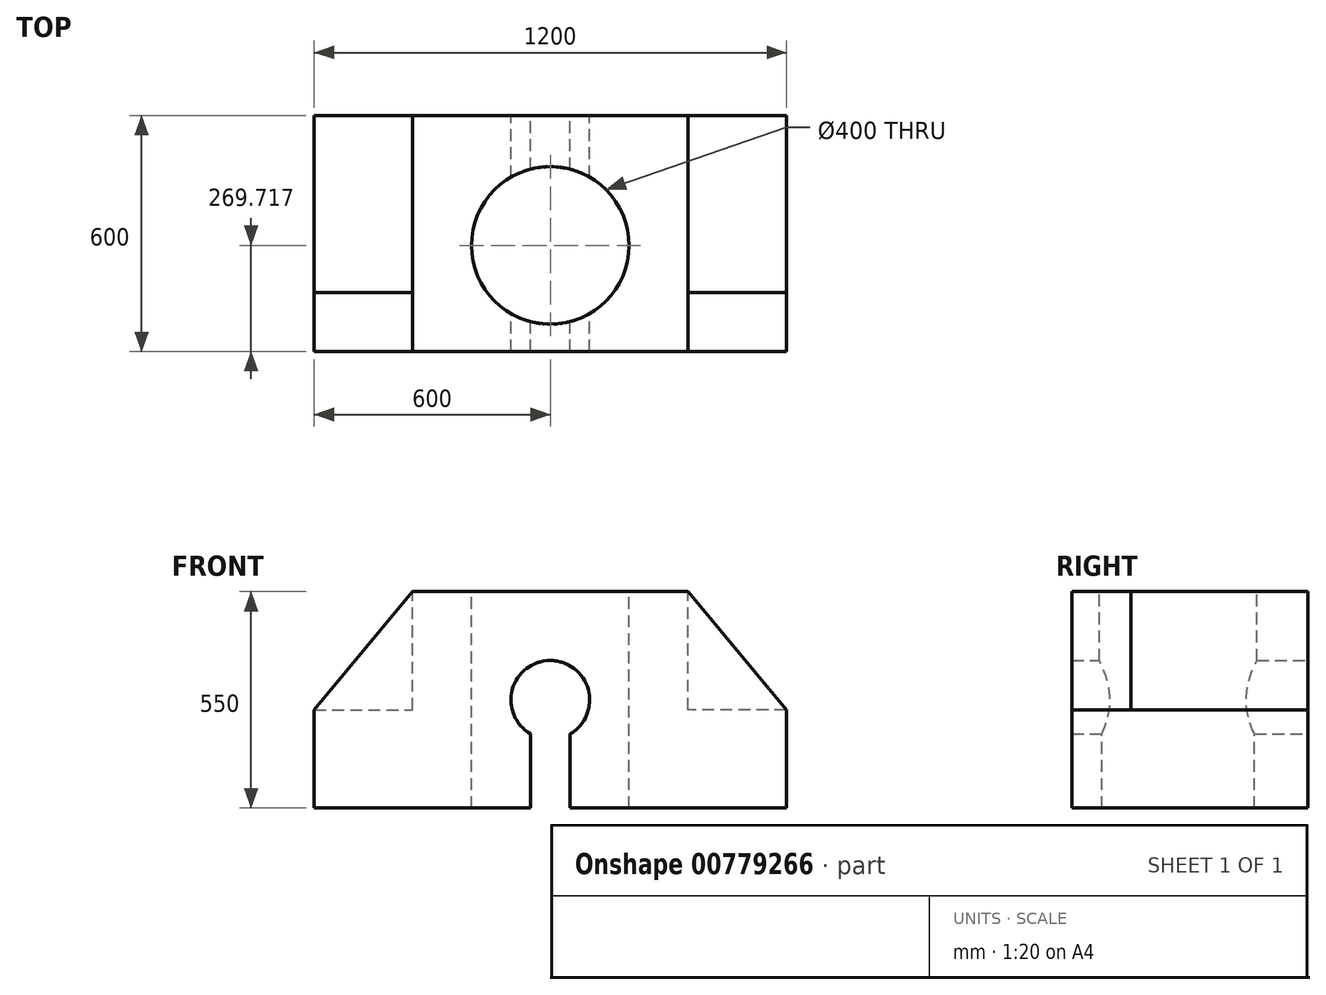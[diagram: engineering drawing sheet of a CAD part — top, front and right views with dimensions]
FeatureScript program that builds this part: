
annotation { "Feature Type Name" : "Feature", "Feature Type Description" : "" }
export const myFeature = defineFeature(function(context is Context, id is Id, definition is map)
    precondition{}
    {
        {
            var Q0;
            Q0=qCreatedBy(makeId("Front.planeOp"),FACE);
            var sketch = newSketch(context, id + "F0", { "sketchPlane" : qUnion([Q0])});
            skLineSegment(sketch, "E0.bottom", {"start": v(-68.7, 40.93) * mm, "end": v(68.7, 40.93) * mm});
            skLineSegment(sketch, "E0.top", {"start": v(-68.7, -40.93) * mm, "end": v(68.7, -40.93) * mm});
            skLineSegment(sketch, "E0.left", {"start": v(-68.7, 40.93) * mm, "end": v(-68.7, -40.93) * mm});
            skLineSegment(sketch, "E0.right", {"start": v(68.7, 40.93) * mm, "end": v(68.7, -40.93) * mm});
            skPoint(sketch, "E0.middle", {"position": v(0, 0) * mm});
            skSolve(sketch);
        }
        {
            var Q0;
            Q0=makeQuery(id+"F0.imprint","IMPRINT",FACE,{"disambiguationData":[TD([[makeQuery(id+"F0.imprint","IMPRINT",EDGE,{"derivedFrom":sQuery(id+"F0.wireOp",EDGE,"E0.bottom")}),-1.0]])]});
            var sketch = newSketch(context, id + "F1", { "sketchPlane" : qUnion([Q0])});
            skLineSegment(sketch, "E1.bottom", {"start": v(600, 275) * mm, "end": v(-600, 275) * mm});
            skLineSegment(sketch, "E1.top", {"start": v(600, -275) * mm, "end": v(-600, -275) * mm});
            skLineSegment(sketch, "E1.left", {"start": v(600, 275) * mm, "end": v(600, -275) * mm});
            skLineSegment(sketch, "E1.right", {"start": v(-600, 275) * mm, "end": v(-600, -275) * mm});
            skPoint(sketch, "E1.middle", {"position": v(0, 0) * mm});
            skPoint(sketch, "E2.middle", {"position": v(0, -275) * mm});
            skPoint(sketch, "E3.orphan", {"position": v(-50, 52.1) * mm});
            skPoint(sketch, "E4.orphan", {"position": v(50, 52.1) * mm});
            skPoint(sketch, "E5.trimOffspring.start.orphan", {"position": v(-50, -448.5) * mm});
            skPoint(sketch, "E6.trimOffspring.start.orphan", {"position": v(50, -450) * mm});
            skPoint(sketch, "E7.top.end.orphan", {"position": v(-50, -602.1) * mm});
            skPoint(sketch, "E7.top.start.orphan", {"position": v(50, -602.1) * mm});
            skPoint(sketch, "E2.right.start.orphan", {"position": v(-50, -100) * mm});
            skPoint(sketch, "E2.left.start.orphan", {"position": v(50, -101.5) * mm});
            skLineSegment(sketch, "E8.right", {"start": v(50, -100) * mm, "end": v(50, -101.5) * mm});
            skArc(sketch, "E9", {"start": v(50, -86.6) * mm, "mid": v(0, 100) * mm, "end": v(-50, -86.6) * mm});
            skPoint(sketch, "E10.trimOffspring.end.orphan", {"position": v(-50, -450) * mm});
            skLineSegment(sketch, "E11.left", {"start": v(-50, -86.6) * mm, "end": v(-50, -275) * mm});
            skLineSegment(sketch, "E11.right", {"start": v(50, -86.6) * mm, "end": v(50, -275) * mm});
            skPoint(sketch, "E12.orphan", {"position": v(50, 0) * mm});
            skPoint(sketch, "E11.bottom.start.orphan", {"position": v(-50, 0) * mm});
            skLineSegment(sketch, "E13.trimOffspring", {"start": v(-50, -448.5) * mm, "end": v(-50, -450) * mm});
            skPoint(sketch, "E11.top.start.orphan", {"position": v(-50, -550) * mm});
            skPoint(sketch, "E14.trimOffspring.end.orphan", {"position": v(50, -550) * mm});
            skSolve(sketch);
        }
        {
            var Q0;
            Q0=makeQuery(id+"F1.imprint","IMPRINT",FACE,{"disambiguationData":[TD([[makeQuery(id+"F1.imprint","IMPRINT",EDGE,{"derivedFrom":sQuery(id+"F1.wireOp",EDGE,"E1.bottom")}),1.0]])]});
            extrude(context, id + "F2", {"entities" : qUnion([Q0]), "depth" : 600 * mm, "offsetDistance" : 25 * mm});
        }
        {
            var Q0;
            Q0=makeQuery(id+"F2.opExtrude","CAP_FACE",FACE,{"disambiguationData":[OSD([sQuery(id+"F1.wireOp",EDGE,"E1.bottom"),sQuery(id+"F1.wireOp",EDGE,"E1.top"),sQuery(id+"F1.wireOp",EDGE,"E1.left"),sQuery(id+"F1.wireOp",EDGE,"E1.right"),sQuery(id+"F1.wireOp",EDGE,"E9"),sQuery(id+"F1.wireOp",EDGE,"E11.left"),sQuery(id+"F1.wireOp",EDGE,"E11.right")])],"isStart":false});
            var sketch = newSketch(context, id + "F3", { "sketchPlane" : qUnion([Q0])});
            skLineSegment(sketch, "E15", {"start": v(-600, -275) * mm, "end": v(-600, -25) * mm});
            skLineSegment(sketch, "E16", {"start": v(-600, -25) * mm, "end": v(-350, -25) * mm});
            skLineSegment(sketch, "E17", {"start": v(-350, -25) * mm, "end": v(-350, 275) * mm});
            skLineSegment(sketch, "E18", {"start": v(600, -275) * mm, "end": v(600, -25) * mm});
            skLineSegment(sketch, "E19", {"start": v(600, -25) * mm, "end": v(350, -25) * mm});
            skLineSegment(sketch, "E20", {"start": v(350, -25) * mm, "end": v(350, 275) * mm});
            skLineSegment(sketch, "E21", {"start": v(350, 275) * mm, "end": v(600, 275) * mm});
            skLineSegment(sketch, "E22", {"start": v(600, 275) * mm, "end": v(600, -25) * mm});
            skLineSegment(sketch, "E23", {"start": v(-350, 275) * mm, "end": v(-600, 275) * mm});
            skLineSegment(sketch, "E24", {"start": v(-600, 275) * mm, "end": v(-600, -25) * mm});
            skSolve(sketch);
        }
        {
            var Q0;
            Q0=makeQuery(id+"F3.imprint","IMPRINT",FACE,{"disambiguationData":[TD([[makeQuery(id+"F3.imprint","IMPRINT",EDGE,{"derivedFrom":sQuery(id+"F3.wireOp",EDGE,"E16")}),1.0]])]});
            var Q1;
            Q1=makeQuery(id+"F3.imprint","IMPRINT",FACE,{"disambiguationData":[TD([[makeQuery(id+"F3.imprint","IMPRINT",EDGE,{"derivedFrom":sQuery(id+"F3.wireOp",EDGE,"E19")}),-1.0]])]});
            extrude(context, id + "F4", {"entities" : qUnion([Q0, Q1]), "operationType" : NewBodyOperationType.REMOVE, "oppositeDirection" : true, "depth" : 600 * mm, "offsetDistance" : 25 * mm});
        }
        {
            var Q0;
            Q0=makeQuery(id+"F2.opExtrude","CAP_FACE",FACE,{"disambiguationData":[OSD([sQuery(id+"F1.wireOp",EDGE,"E1.bottom"),sQuery(id+"F1.wireOp",EDGE,"E1.top"),sQuery(id+"F1.wireOp",EDGE,"E1.left"),sQuery(id+"F1.wireOp",EDGE,"E1.right"),sQuery(id+"F1.wireOp",EDGE,"E9"),sQuery(id+"F1.wireOp",EDGE,"E11.left"),sQuery(id+"F1.wireOp",EDGE,"E11.right")])],"isStart":false});
            var sketch = newSketch(context, id + "F5", { "sketchPlane" : qUnion([Q0])});
            skLineSegment(sketch, "E25", {"start": v(-600, -25) * mm, "end": v(-350, 275) * mm});
            skSolve(sketch);
        }
        {
            var Q0;
            Q0=makeQuery(id+"F5.imprint","IMPRINT",FACE,{"disambiguationData":[TD([[makeQuery(id+"F5.imprint","IMPRINT",EDGE,{"derivedFrom":sQuery(id+"F5.wireOp",EDGE,"E25")}),-1.0]])]});
            extrude(context, id + "F6", {"entities" : qUnion([Q0]), "operationType" : NewBodyOperationType.ADD, "oppositeDirection" : true, "depth" : 150 * mm, "offsetDistance" : 25 * mm});
        }
        {
            var Q0;
            Q0=makeQuery(id+"F6.boolean.opBoolean","MERGE",FACE,{"derivedFrom":[makeQuery(id+"F2.opExtrude","CAP_FACE",FACE,{"disambiguationData":[OSD([sQuery(id+"F1.wireOp",EDGE,"E1.bottom"),sQuery(id+"F1.wireOp",EDGE,"E1.top"),sQuery(id+"F1.wireOp",EDGE,"E1.left"),sQuery(id+"F1.wireOp",EDGE,"E1.right"),sQuery(id+"F1.wireOp",EDGE,"E9"),sQuery(id+"F1.wireOp",EDGE,"E11.left"),sQuery(id+"F1.wireOp",EDGE,"E11.right")])],"isStart":false}),makeQuery(id+"F6.opExtrude","CAP_FACE",FACE,{"disambiguationData":[OSD([sQuery(id+"F3.wireOp",EDGE,"E16"),sQuery(id+"F3.wireOp",EDGE,"E17"),sQuery(id+"F5.wireOp",EDGE,"E25")])],"isStart":true})]});
            var sketch = newSketch(context, id + "F7", { "sketchPlane" : qUnion([Q0])});
            skLineSegment(sketch, "E26", {"start": v(600, -25) * mm, "end": v(350, 275) * mm});
            skSolve(sketch);
        }
        {
            var Q0;
            Q0=makeQuery(id+"F7.imprint","IMPRINT",FACE,{"disambiguationData":[TD([[makeQuery(id+"F7.imprint","IMPRINT",EDGE,{"derivedFrom":sQuery(id+"F7.wireOp",EDGE,"E26")}),1.0]])]});
            extrude(context, id + "F8", {"entities" : qUnion([Q0]), "operationType" : NewBodyOperationType.ADD, "oppositeDirection" : true, "depth" : 150 * mm, "offsetDistance" : 25 * mm});
        }
        {
            var Q0;
            Q0=makeQuery(id+"F2.opExtrude","SWEPT_FACE",FACE,{"disambiguationData":[OSD([sQuery(id+"F1.wireOp",EDGE,"E1.bottom")])]});
            var sketch = newSketch(context, id + "F9", { "sketchPlane" : qUnion([Q0])});
            skCircle(sketch, "E27", {"center": v(0, -330.28) * mm, "radius": 200 * mm});
            skPoint(sketch, "E27.centerSnap0", {"position": v(0, 0) * mm});
            skSolve(sketch);
        }
        {
            var Q0;
            Q0=makeQuery(id+"F9.imprint","IMPRINT",FACE,{"disambiguationData":[TD([[makeQuery(id+"F9.imprint","IMPRINT",EDGE,{"derivedFrom":sQuery(id+"F9.wireOp",EDGE,"E27")}),1.0]])]});
            extrude(context, id + "F10", {"entities" : qUnion([Q0]), "operationType" : NewBodyOperationType.REMOVE, "endBound" : BoundingType.THROUGH_ALL, "oppositeDirection" : true, "depth" : 25 * mm, "offsetDistance" : 25 * mm});
        }
    });
